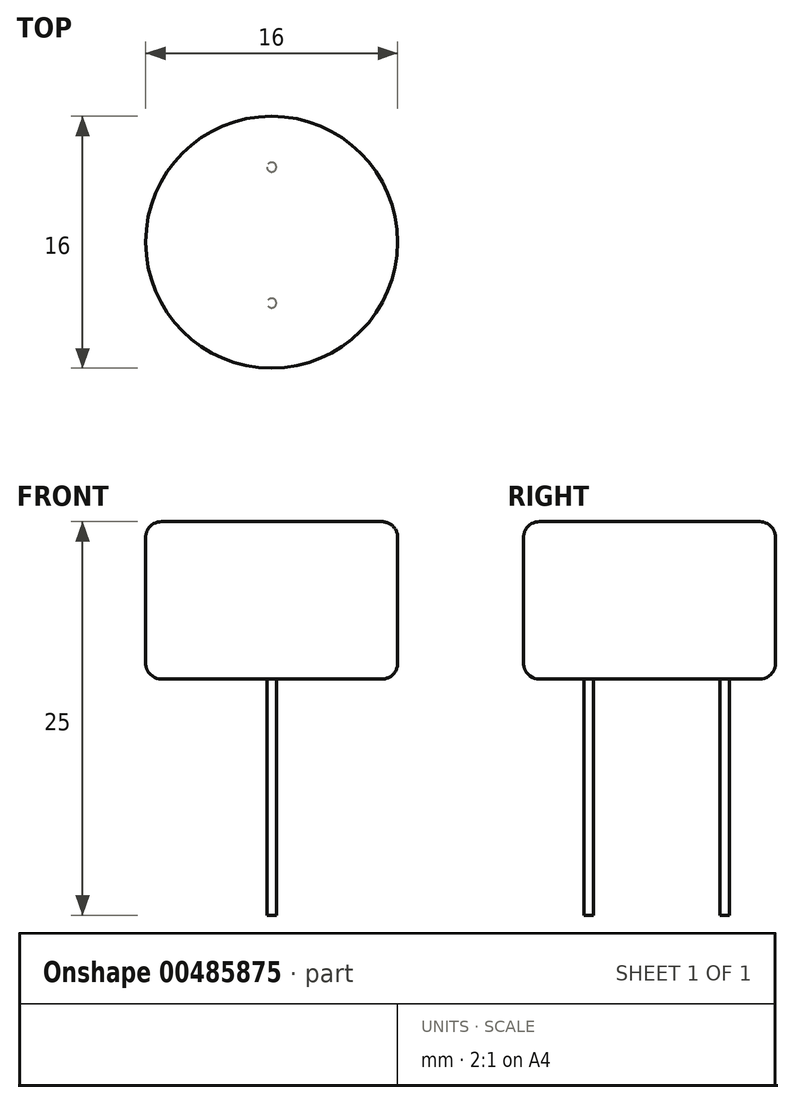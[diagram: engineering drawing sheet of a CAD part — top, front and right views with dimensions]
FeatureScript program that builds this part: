
annotation { "Feature Type Name" : "Feature", "Feature Type Description" : "" }
export const myFeature = defineFeature(function(context is Context, id is Id, definition is map)
    precondition{}
    {
        {
            var Q0;
            Q0=qCreatedBy(makeId("Top.planeOp"),FACE);
            var sketch = newSketch(context, id + "F0", { "sketchPlane" : qUnion([Q0])});
            skCircle(sketch, "E0", {"center": v(0, 0) * mm, "radius": 8 * mm});
            skSolve(sketch);
        }
        {
            var Q0;
            Q0 = qSketchRegion(id + "F0", true);
            var Q1;
            Q1=makeQuery(id+"F0.imprint","IMPRINT",FACE,{"disambiguationData":[TD([[makeQuery(id+"F0.imprint","IMPRINT",EDGE,{"derivedFrom":sQuery(id+"F0.wireOp",EDGE,"E0")}),1.0]])]});
            extrude(context, id + "F1", {"entities" : qUnion([Q0, Q1]), "depth" : 10 * mm});
        }
        {
            var Q0;
            Q0=makeQuery(id+"F1.opExtrude","CAP_FACE",FACE,{"disambiguationData":[OSD([sQuery(id+"F0.wireOp",EDGE,"E0")])],"isStart":true});
            var sketch = newSketch(context, id + "F2", { "sketchPlane" : qUnion([Q0])});
            skCircle(sketch, "E1", {"center": v(0, 3.87) * mm, "radius": 0.3 * mm});
            skCircle(sketch, "E2", {"center": v(0, -4.77) * mm, "radius": 0.3 * mm});
            skSolve(sketch);
        }
        {
            var Q0;
            Q0 = qSketchRegion(id + "F2", true);
            extrude(context, id + "F3", {"entities" : qUnion([Q0]), "operationType" : NewBodyOperationType.ADD, "depth" : 15 * mm});
        }
        {
            var Q0;
            Q0=makeQuery(id+"F1.opExtrude","CAP_EDGE",EDGE,{"disambiguationData":[OSD([sQuery(id+"F0.wireOp",EDGE,"E0")])],"isStart":false});
            var Q1;
            Q1=makeQuery(id+"F1.opExtrude","CAP_EDGE",EDGE,{"disambiguationData":[OSD([sQuery(id+"F0.wireOp",EDGE,"E0")])],"isStart":true});
            fillet(context, id + "F4", {"entities" : qUnion([Q0, Q1]), "radius" : 1 * mm, "tangentPropagation" : true, "allowEdgeOverflow" : false});
        }
    });
